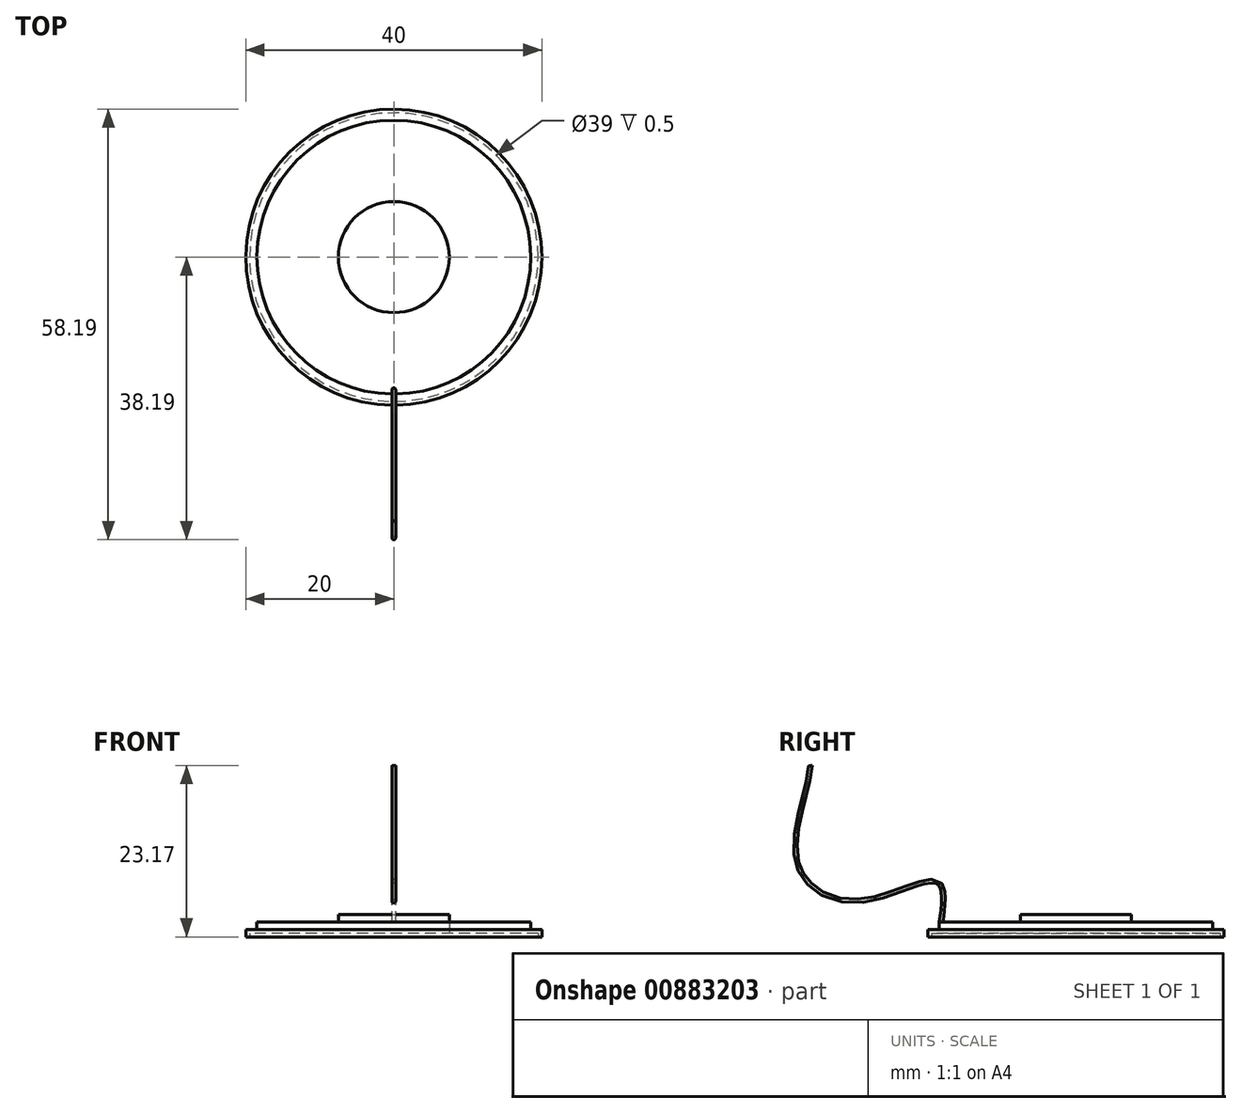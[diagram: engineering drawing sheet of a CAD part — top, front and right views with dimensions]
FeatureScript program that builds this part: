
annotation { "Feature Type Name" : "Feature", "Feature Type Description" : "" }
export const myFeature = defineFeature(function(context is Context, id is Id, definition is map)
    precondition{}
    {
        {
            var Q0;
            Q0=qCreatedBy(makeId("Top.planeOp"),FACE);
            var sketch = newSketch(context, id + "F0", { "sketchPlane" : qUnion([Q0])});
            skCircle(sketch, "E0", {"center": v(0, 0) * mm, "radius": 20 * mm});
            skSolve(sketch);
        }
        {
            var Q0;
            Q0=makeQuery(id+"F0.imprint","IMPRINT",FACE,{"disambiguationData":[TD([[makeQuery(id+"F0.imprint","IMPRINT",EDGE,{"derivedFrom":sQuery(id+"F0.wireOp",EDGE,"E0")}),1.0]])]});
            extrude(context, id + "F1", {"entities" : qUnion([Q0]), "depth" : 1 * mm, "offsetDistance" : 25 * mm});
        }
        {
            var Q0;
            Q0=makeQuery(id+"F1.opExtrude","CAP_FACE",FACE,{"disambiguationData":[OSD([sQuery(id+"F0.wireOp",EDGE,"E0")])],"isStart":false});
            var sketch = newSketch(context, id + "F2", { "sketchPlane" : qUnion([Q0])});
            skCircle(sketch, "E1", {"center": v(0, 0) * mm, "radius": 18.5 * mm});
            skSolve(sketch);
        }
        {
            var Q0;
            Q0=makeQuery(id+"F2.imprint","IMPRINT",FACE,{"disambiguationData":[TD([[makeQuery(id+"F2.imprint","IMPRINT",EDGE,{"derivedFrom":sQuery(id+"F2.wireOp",EDGE,"E1")}),1.0]])]});
            extrude(context, id + "F3", {"entities" : qUnion([Q0]), "depth" : 1 * mm, "offsetDistance" : 25 * mm});
        }
        {
            var Q0;
            Q0=makeQuery(id+"F3.opExtrude","CAP_FACE",FACE,{"disambiguationData":[OSD([sQuery(id+"F2.wireOp",EDGE,"E1")])],"isStart":false});
            var sketch = newSketch(context, id + "F4", { "sketchPlane" : qUnion([Q0])});
            skCircle(sketch, "E2", {"center": v(0, 0) * mm, "radius": 7.5 * mm});
            skSolve(sketch);
        }
        {
            var Q0;
            Q0 = qSketchRegion(id + "F4", true);
            extrude(context, id + "F5", {"entities" : qUnion([Q0]), "depth" : 1 * mm, "offsetDistance" : 25 * mm, "hasSecondDirection" : true, "secondDirectionOppositeDirection" : true, "secondDirectionDepth" : 2 * mm});
        }
        {
            var Q0;
            Q0=makeQuery(id+"F1.opExtrude","CAP_FACE",FACE,{"disambiguationData":[OSD([sQuery(id+"F0.wireOp",EDGE,"E0")])],"isStart":true});
            shell(context, id + "F6", {"entities" : qUnion([Q0]), "thickness" : 0.5 * mm});
        }
        {
            var Q0;
            Q0=makeQuery(id+"F3.opExtrude","CAP_FACE",FACE,{"disambiguationData":[OSD([sQuery(id+"F2.wireOp",EDGE,"E1")])],"isStart":false});
            var sketch = newSketch(context, id + "F7", { "sketchPlane" : qUnion([Q0])});
            skCircle(sketch, "E3", {"center": v(0, -18.25) * mm, "radius": 0.25 * mm});
            skSolve(sketch);
        }
        {
            var Q0;
            Q0=qCreatedBy(makeId("Right.planeOp"),FACE);
            var sketch = newSketch(context, id + "F8", { "sketchPlane" : qUnion([Q0])});
            skFitSpline(sketch, "E4", {"points": [v(-18, 2) * mm, v(-18.22, 7.31) * mm, v(-28.98, 5.14) * mm, v(-37.5, 10.32) * mm, v(-35.65, 23.17) * mm], "startDerivative": vector(1.89, 9.9) * mm, "endDerivative": vector(0.94, 33.03) * mm});
            skSolve(sketch);
        }
        {
            var Q0;
            Q0 = qSketchRegion(id + "F7", true);
            var Q1;
            Q1 = qConstructionFilter(qBodyType(qCreatedBy(id + "F8" ,EDGE), BodyType.WIRE), ConstructionObject.NO);
            sweep(context, id + "F9", {"operationType" : NewBodyOperationType.ADD, "profiles" : qUnion([Q0]), "path" : qUnion([Q1])});
        }
    });
